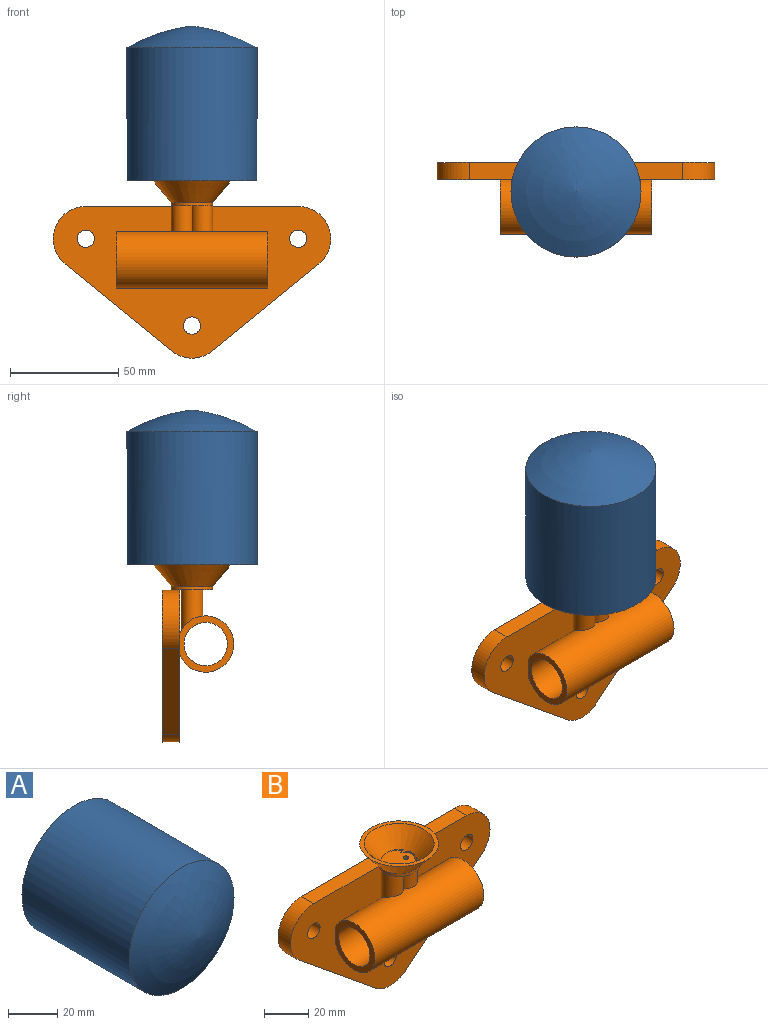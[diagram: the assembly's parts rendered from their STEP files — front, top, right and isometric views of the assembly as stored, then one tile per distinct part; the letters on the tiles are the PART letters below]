
ASSEMBLY  parts=2 mates=1
PART A: 7 faces, bbox 60x71.5x60 mm
  f0: cylinder r=30mm len=61.5mm, axis (0,1,0), area 11592.5mm2, adj f3,f6
  f1: plane 57x57mm, normal (0,-1,0), area 1758.4mm2, adj f2,f5
  f2: cylinder r=15.89mm len=31.78mm, axis (0,-1,0), area 149.8mm2, adj f1,f3
  f3: plane 60x60mm, normal (0,1,0), area 2034.1mm2, adj f0,f2
  f4: plane 57x57mm, normal (0,1,0), area 2551.8mm2, adj f5
  f5: cylinder r=28.5mm len=58.5mm, axis (0,1,0), area 10475.6mm2, adj f1,f4
  f6: revolved ~60x60mm, area 3067.4mm2, adj f0
PART B: 42 faces, bbox 128x37.2x81.7 mm
  f0: plane 18x17mm, normal (0,0,1), area 227.1mm2, adj f29,f30,f32,f33,f34,f35,f36,f37
  f1: cylinder r=5mm len=18.58mm, axis (0,0,-1), area 391.7mm2, adj f4,f17,f22,f23
  f2: cylinder r=4mm len=20mm, axis (0,0,-1), area 442.7mm2, adj f5,f21,f26
  f3: cylinder r=4mm len=20mm, axis (0,0,-1), area 442.7mm2, adj f5,f20,f25
  f4: cylinder r=5mm len=18.58mm, axis (0,0,-1), area 391.7mm2, adj f1,f17,f22,f23
  f5: cylinder r=10mm len=70mm, axis (-1,0,0), area 4286.5mm2, adj f2,f3,f18,f19,f20,f21
  f6: plane 98x8mm, normal (0,0,1), area 784mm2, adj f7,f14,f15,f16
  f7: cylinder r=15mm len=26.62mm, axis (0,1,0), area 294.8mm2, adj f6,f8,f15,f16
  f8: plane 49x40mm, normal (-0.63,0,-0.77), area 506mm2, adj f7,f9,f15,f16
  f9: cylinder r=15mm len=18.97mm, axis (0,1,0), area 164.3mm2, adj f8,f10,f15,f16
  f10: plane 49x40mm, normal (0.63,0,-0.77), area 506mm2, adj f9,f14,f15,f16
  f11: cylinder r=4mm len=8mm, axis (0,1,0), area 201.1mm2, adj f15,f16
  f12: cylinder r=4mm len=8mm, axis (0,1,0), area 201.1mm2, adj f15,f16
  f13: cylinder r=4mm len=8mm, axis (0,1,0), area 201.1mm2, adj f15,f16
  f14: cylinder r=15mm len=26.62mm, axis (0,1,0), area 294.8mm2, adj f6,f10,f15,f16
  f15: plane 128x70mm, normal (0,-1,0), area 5183.7mm2, adj f6,f7,f8,f9,f10,f11,f12,f13
  f16: plane 128x70mm, normal (0,1,0), area 5883.7mm2, adj f6,f7,f8,f9,f10,f11,f12,f13
  f17: cylinder r=13mm len=70mm, axis (-1,0,0), area 4812.2mm2, adj f1,f4,f15,f18,f19
  f18: plane 26x25mm, normal (1,0,0), area 210.1mm2, adj f5,f15,f17
  f19: plane 26x25mm, normal (-1,0,0), area 210.1mm2, adj f5,f15,f17
  f20: plane 6.47x1.65mm, normal (0,0,1), area 7.4mm2, adj f3,f5
  f21: plane 6.47x1.65mm, normal (0,0,1), area 7.4mm2, adj f2,f5
  f22: plane 19x9.5mm, normal (0,0,-1), area 64.7mm2, adj f1,f4,f24
  f23: plane 19x9.5mm, normal (0,0,-1), area 64.7mm2, adj f1,f4,f24
  f24: cylinder r=9.5mm len=19mm, axis (0,0,-1), area 89.5mm2, adj f22,f23,f27
  f25: plane 8x8mm, normal (0,0,-1), area 45mm2, adj f3,f41
  f26: plane 8x8mm, normal (0,0,-1), area 45mm2, adj f2,f40
  f27: cone r=9.5mm half-angle=40deg, axis (0,0,1), area 1123.3mm2, adj f24,f28
  f28: plane 35.78x35.78mm, normal (0,0,1), area 212.3mm2, adj f27,f29
  f29: cone r=7.5mm half-angle=40deg, axis (0,0,1), area 911.5mm2, adj f0,f28,f30,f31,f32,f33,f34,f35
  f30: cylinder r=4mm len=6.65mm, axis (0,0,-1), area 4.7mm2, adj f0,f29,f31
  f31: cone r=9mm half-angle=40deg, axis (0,0,-1), area 1mm2, adj f29,f30
  f32: cylinder r=5mm len=2.75mm, axis (0,0,-1), area 1.5mm2, adj f0,f29,f34
  f33: cylinder r=5mm len=2.75mm, axis (0,0,-1), area 1.5mm2, adj f0,f29,f34
  f34: cone r=9mm half-angle=40deg, axis (0,0,-1), area 22.5mm2, adj f0,f29,f32,f33
  f35: cylinder r=5mm len=2.75mm, axis (0,0,-1), area 1.5mm2, adj f0,f29,f37
  f36: cylinder r=5mm len=2.75mm, axis (0,0,-1), area 1.5mm2, adj f0,f29,f37
  f37: cone r=9mm half-angle=40deg, axis (0,0,-1), area 22.5mm2, adj f0,f29,f35,f36
  f38: cylinder r=4mm len=6.65mm, axis (0,0,-1), area 4.7mm2, adj f0,f29,f39
  f39: cone r=9mm half-angle=40deg, axis (0,0,-1), area 1mm2, adj f29,f38
  f40: cylinder r=1.29mm len=2.58mm, axis (0,0,1), area 12.2mm2, adj f0,f26
  f41: cylinder r=1.29mm len=2.58mm, axis (0,0,1), area 12.2mm2, adj f0,f25
PLACE A rot(axis=(-1,0,0),90deg) t=(0,-13.69,58)mm
PLACE B at identity
MATE fastened A.f2 <-> B.f24  axis (0,0,-1) through (0,-13.69,56.5)mm
